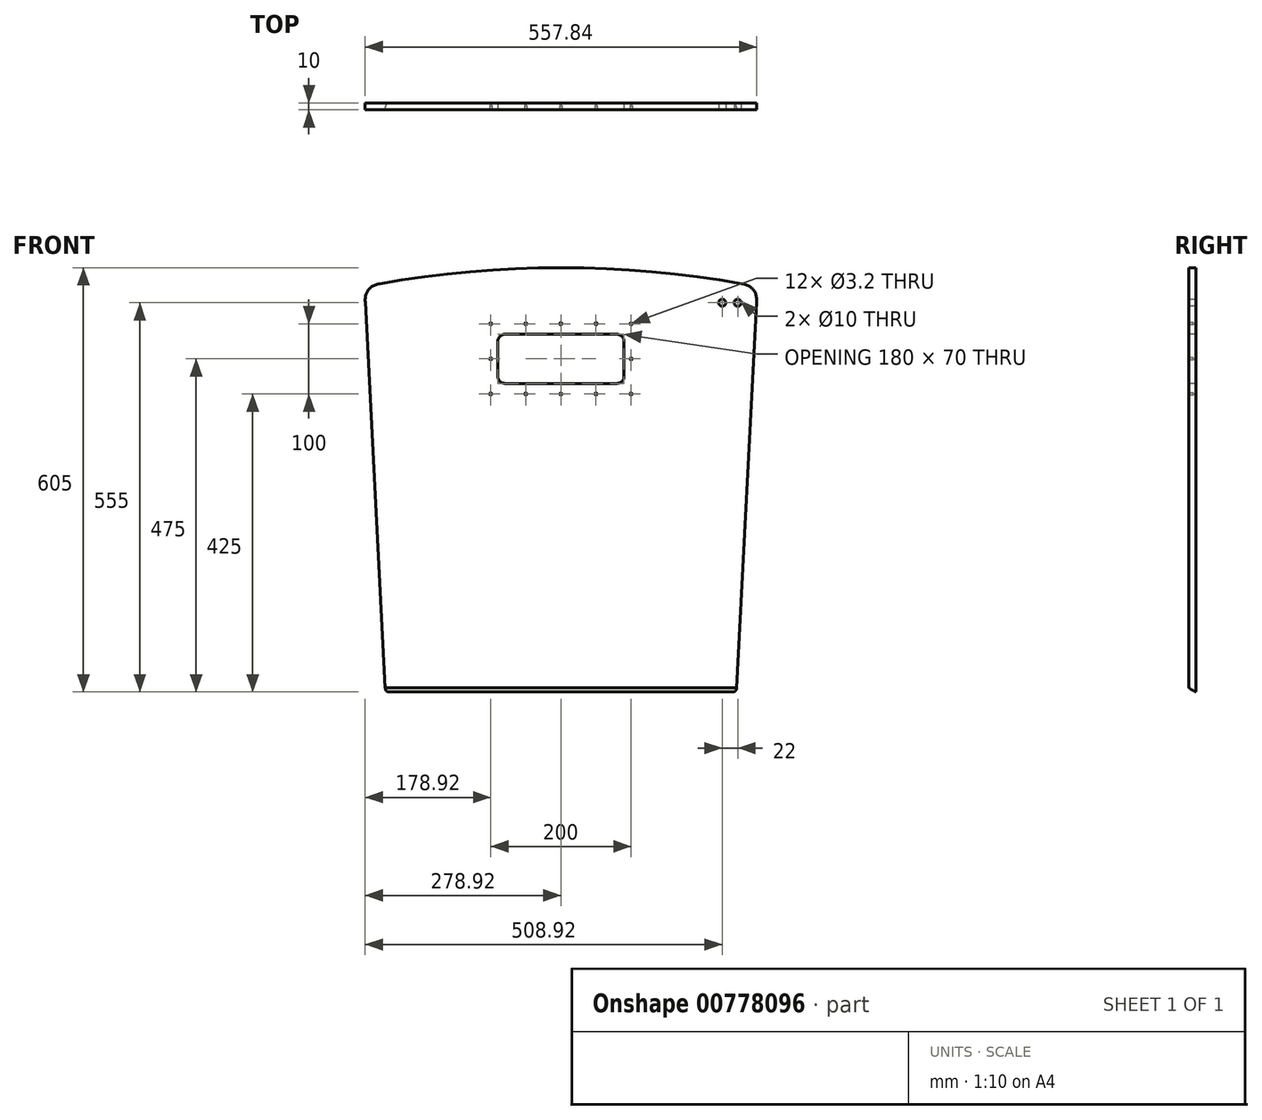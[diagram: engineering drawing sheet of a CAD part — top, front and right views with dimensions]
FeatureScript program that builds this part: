
annotation { "Feature Type Name" : "Feature", "Feature Type Description" : "" }
export const myFeature = defineFeature(function(context is Context, id is Id, definition is map)
    precondition{}
    {
        {
            var Q0;
            Q0=qCreatedBy(makeId("Front.planeOp"),FACE);
            var sketch = newSketch(context, id + "F0", { "sketchPlane" : qUnion([Q0])});
            skLineSegment(sketch, "E0", {"start": v(0, 0) * mm, "end": v(500, 0) * mm});
            skLineSegment(sketch, "E1", {"start": v(500, 0) * mm, "end": v(530, 578) * mm});
            skLineSegment(sketch, "E2", {"start": v(-30, 578) * mm, "end": v(0, 0) * mm});
            skPoint(sketch, "E3.center.orphan", {"position": v(250, 0) * mm});
            skArc(sketch, "E4", {"start": v(530, 578) * mm, "mid": v(250, 605) * mm, "end": v(-30, 578) * mm});
            skLineSegment(sketch, "E5", {"start": v(-30, 578) * mm, "end": v(530, 578) * mm, "construction": true});
            skLineSegment(sketch, "E6", {"start": v(250, -860.35) * mm, "end": v(250, 0) * mm, "construction": true});
            skSolve(sketch);
        }
        {
            var Q0;
            Q0=makeQuery(id+"F0.imprint","IMPRINT",FACE,{"disambiguationData":[TD([[makeQuery(id+"F0.imprint","IMPRINT",EDGE,{"derivedFrom":sQuery(id+"F0.wireOp",EDGE,"E0")}),1.0]])]});
            extrude(context, id + "F1", {"entities" : qUnion([Q0]), "depth" : 10 * mm, "offsetDistance" : 25 * mm});
        }
        {
            var Q0;
            Q0=makeQuery(id+"F1.opExtrude","CAP_FACE",FACE,{"disambiguationData":[OSD([sQuery(id+"F0.wireOp",EDGE,"E0"),sQuery(id+"F0.wireOp",EDGE,"E1"),sQuery(id+"F0.wireOp",EDGE,"E3"),sQuery(id+"F0.wireOp",EDGE,"E2")])],"isStart":false});
            var sketch = newSketch(context, id + "F2", { "sketchPlane" : qUnion([Q0])});
            skLineSegment(sketch, "E7.bottom", {"start": v(160, 510) * mm, "end": v(340, 510) * mm});
            skLineSegment(sketch, "E7.top", {"start": v(160, 440) * mm, "end": v(340, 440) * mm});
            skLineSegment(sketch, "E7.left", {"start": v(160, 510) * mm, "end": v(160, 440) * mm});
            skLineSegment(sketch, "E7.right", {"start": v(340, 510) * mm, "end": v(340, 440) * mm});
            skLineSegment(sketch, "E8", {"start": v(250, 440) * mm, "end": v(250, 0) * mm, "construction": true});
            skSolve(sketch);
        }
        {
            var Q0;
            Q0=makeQuery(id+"F2.imprint","IMPRINT",FACE,{"disambiguationData":[TD([[makeQuery(id+"F2.imprint","IMPRINT",EDGE,{"derivedFrom":sQuery(id+"F2.wireOp",EDGE,"E7.bottom")}),-1.0]])]});
            extrude(context, id + "F3", {"entities" : qUnion([Q0]), "operationType" : NewBodyOperationType.REMOVE, "endBound" : BoundingType.THROUGH_ALL, "oppositeDirection" : true, "depth" : 25 * mm, "offsetDistance" : 25 * mm});
        }
        {
            var Q0;
            Q0=makeQuery(id+"F1.opExtrude","SWEPT_EDGE",EDGE,{"disambiguationData":[OSD([sQuery(id+"F0.wireOp",EDGE,"E2"),sQuery(id+"F0.wireOp",EDGE,"E4")])]});
            var Q1;
            Q1=makeQuery(id+"F1.opExtrude","SWEPT_EDGE",EDGE,{"disambiguationData":[OSD([sQuery(id+"F0.wireOp",EDGE,"E1"),sQuery(id+"F0.wireOp",EDGE,"E4")])]});
            fillet(context, id + "F4", {"entities" : qUnion([Q0, Q1]), "radius" : 25 * mm, "rho" : 0.5, "crossSection" : FilletCrossSection.CONIC, "allowEdgeOverflow" : false});
        }
        {
            var Q0;
            Q0=makeQuery(id+"F1.opExtrude","SWEPT_EDGE",EDGE,{"disambiguationData":[OSD([sQuery(id+"F0.wireOp",EDGE,"E0"),sQuery(id+"F0.wireOp",EDGE,"E1")])]});
            var Q1;
            Q1=makeQuery(id+"F1.opExtrude","SWEPT_EDGE",EDGE,{"disambiguationData":[OSD([sQuery(id+"F0.wireOp",EDGE,"E0"),sQuery(id+"F0.wireOp",EDGE,"E2")])]});
            fillet(context, id + "F5", {"entities" : qUnion([Q0, Q1]), "radius" : 5 * mm, "tangentPropagation" : true, "allowEdgeOverflow" : false});
        }
        {
            var Q0;
            Q0=makeQuery(id+"F1.opExtrude","CAP_EDGE",EDGE,{"disambiguationData":[OSD([sQuery(id+"F0.wireOp",EDGE,"E0")])],"isStart":false});
            chamfer(context, id + "F6", {"entities" : qUnion([Q0]), "chamferType" : ChamferType.OFFSET_ANGLE, "width" : 5.7 * mm, "oppositeDirection" : false, "angle" : 60 * degree});
        }
        {
            var Q0;
            Q0=makeQuery(id+"F3.boolean.opBoolean","COPY",EDGE,{"derivedFrom":makeQuery(id+"F3.opExtrude","SWEPT_EDGE",EDGE,{"disambiguationData":[OSD([sQuery(id+"F2.wireOp",EDGE,"E7.bottom"),sQuery(id+"F2.wireOp",EDGE,"E7.right")])]})});
            var Q1;
            Q1=makeQuery(id+"F3.boolean.opBoolean","COPY",EDGE,{"derivedFrom":makeQuery(id+"F3.opExtrude","SWEPT_EDGE",EDGE,{"disambiguationData":[OSD([sQuery(id+"F2.wireOp",EDGE,"E7.bottom"),sQuery(id+"F2.wireOp",EDGE,"E7.left")])]})});
            var Q2;
            Q2=makeQuery(id+"F3.boolean.opBoolean","COPY",EDGE,{"derivedFrom":makeQuery(id+"F3.opExtrude","SWEPT_EDGE",EDGE,{"disambiguationData":[OSD([sQuery(id+"F2.wireOp",EDGE,"E7.top"),sQuery(id+"F2.wireOp",EDGE,"E7.left")])]})});
            var Q3;
            Q3=makeQuery(id+"F3.boolean.opBoolean","COPY",EDGE,{"derivedFrom":makeQuery(id+"F3.opExtrude","SWEPT_EDGE",EDGE,{"disambiguationData":[OSD([sQuery(id+"F2.wireOp",EDGE,"E7.top"),sQuery(id+"F2.wireOp",EDGE,"E7.right")])]})});
            fillet(context, id + "F7", {"entities" : qUnion([Q0, Q1, Q2, Q3]), "radius" : 10 * mm, "tangentPropagation" : true, "allowEdgeOverflow" : false});
        }
        {
            var Q0;
            Q0=makeQuery(id+"F1.opExtrude","CAP_FACE",FACE,{"disambiguationData":[OSD([sQuery(id+"F0.wireOp",EDGE,"E0"),sQuery(id+"F0.wireOp",EDGE,"E1"),sQuery(id+"F0.wireOp",EDGE,"E3"),sQuery(id+"F0.wireOp",EDGE,"E2")])],"isStart":false});
            var sketch = newSketch(context, id + "F8", { "sketchPlane" : qUnion([Q0])});
            skLineSegment(sketch, "E9.bottom", {"start": v(150, 525) * mm, "end": v(350, 525) * mm});
            skLineSegment(sketch, "E9.top", {"start": v(150, 425) * mm, "end": v(350, 425) * mm});
            skLineSegment(sketch, "E9.left", {"start": v(150, 525) * mm, "end": v(150, 425) * mm});
            skLineSegment(sketch, "E9.right", {"start": v(350, 525) * mm, "end": v(350, 425) * mm});
            skLineSegment(sketch, "E10.bottom", {"start": v(200, 525) * mm, "end": v(300, 525) * mm});
            skLineSegment(sketch, "E10.top", {"start": v(200, 425) * mm, "end": v(300, 425) * mm});
            skLineSegment(sketch, "E10.left", {"start": v(200, 525) * mm, "end": v(200, 425) * mm});
            skLineSegment(sketch, "E10.right", {"start": v(300, 525) * mm, "end": v(300, 425) * mm});
            skLineSegment(sketch, "E11", {"start": v(250, 510) * mm, "end": v(250, 440) * mm});
            skLineSegment(sketch, "E12", {"start": v(160, 475) * mm, "end": v(340, 475) * mm});
            skLineSegment(sketch, "E13", {"start": v(250, 510) * mm, "end": v(250, 525) * mm});
            skLineSegment(sketch, "E14", {"start": v(250, 440) * mm, "end": v(250, 425) * mm});
            skLineSegment(sketch, "E15", {"start": v(340, 475) * mm, "end": v(350, 475) * mm});
            skLineSegment(sketch, "E16", {"start": v(160, 475) * mm, "end": v(150, 475) * mm});
            skSolve(sketch);
        }
        {
            var Q0;
            Q0=sQuery(id+"F8.wireOp",VERTEX,"E9.bottom.start");
            var Q1;
            Q1=sQuery(id+"F8.wireOp",VERTEX,"E10.bottom.start");
            var Q2;
            Q2=sQuery(id+"F8.wireOp",VERTEX,"E13.end");
            var Q3;
            Q3=sQuery(id+"F8.wireOp",VERTEX,"E14.end");
            var Q4;
            Q4=sQuery(id+"F8.wireOp",VERTEX,"E10.top.start");
            var Q5;
            Q5=sQuery(id+"F8.wireOp",VERTEX,"E9.top.start");
            var Q6;
            Q6=sQuery(id+"F8.wireOp",VERTEX,"E16.end");
            var Q7;
            Q7=sQuery(id+"F8.wireOp",VERTEX,"E9.bottom.end");
            var Q8;
            Q8=sQuery(id+"F8.wireOp",VERTEX,"E15.end");
            var Q9;
            Q9=sQuery(id+"F8.wireOp",VERTEX,"E9.top.end");
            var Q10;
            Q10=sQuery(id+"F8.wireOp",VERTEX,"E10.top.end");
            var Q11;
            Q11=sQuery(id+"F8.wireOp",VERTEX,"E10.bottom.end");
            var Q12;
            Q12=makeQuery(id+"F1.opExtrude","SWEPT_BODY",BODY,{"disambiguationData":[OSD([sQuery(id+"F0.wireOp",EDGE,"E0"),sQuery(id+"F0.wireOp",EDGE,"E1"),sQuery(id+"F0.wireOp",EDGE,"E3"),sQuery(id+"F0.wireOp",EDGE,"E2")])]});
            hole(context, id + "F9", {"style" : HoleStyle.SIMPLE, "endStyle" : HoleEndStyle.BLIND, "holeDiameter" : 3.2 * mm, "majorDiameter" : 5 * mm, "holeDepth" : 6 * mm, "isTappedThrough" : true, "tappedDepth" : 12 * mm, "tapClearance" : 3, "locations" : qUnion([Q0, Q1, Q2, Q3, Q4, Q5, Q6, Q7, Q8, Q9, Q10, Q11]), "scope" : qUnion([Q12])});
        }
        {
            var Q0;
            Q0=makeQuery(id+"F1.opExtrude","CAP_FACE",FACE,{"disambiguationData":[OSD([sQuery(id+"F0.wireOp",EDGE,"E0"),sQuery(id+"F0.wireOp",EDGE,"E1"),sQuery(id+"F0.wireOp",EDGE,"E3"),sQuery(id+"F0.wireOp",EDGE,"E2")])],"isStart":false});
            var sketch = newSketch(context, id + "F10", { "sketchPlane" : qUnion([Q0])});
            skLineSegment(sketch, "E17", {"start": v(480, 555) * mm, "end": v(502, 555) * mm});
            skLineSegment(sketch, "E18", {"start": v(480, 555) * mm, "end": v(250, 555) * mm, "construction": true});
            skLineSegment(sketch, "E19", {"start": v(250, 555) * mm, "end": v(250, 525) * mm, "construction": true});
            skSolve(sketch);
        }
        {
            var Q0;
            Q0=sQuery(id+"F10.wireOp",VERTEX,"E17.start");
            var Q1;
            Q1=sQuery(id+"F10.wireOp",VERTEX,"E17.end");
            var Q2;
            Q2=makeQuery(id+"F1.opExtrude","SWEPT_BODY",BODY,{"disambiguationData":[OSD([sQuery(id+"F0.wireOp",EDGE,"E0"),sQuery(id+"F0.wireOp",EDGE,"E1"),sQuery(id+"F0.wireOp",EDGE,"E2"),sQuery(id+"F0.wireOp",EDGE,"E4")])]});
            hole(context, id + "F11", {"style" : HoleStyle.SIMPLE, "endStyle" : HoleEndStyle.THROUGH, "holeDiameter" : 10 * mm, "majorDiameter" : 5 * mm, "isTappedThrough" : true, "tappedDepth" : 12 * mm, "tapClearance" : 3, "locations" : qUnion([Q0, Q1]), "scope" : qUnion([Q2])});
        }
    });
